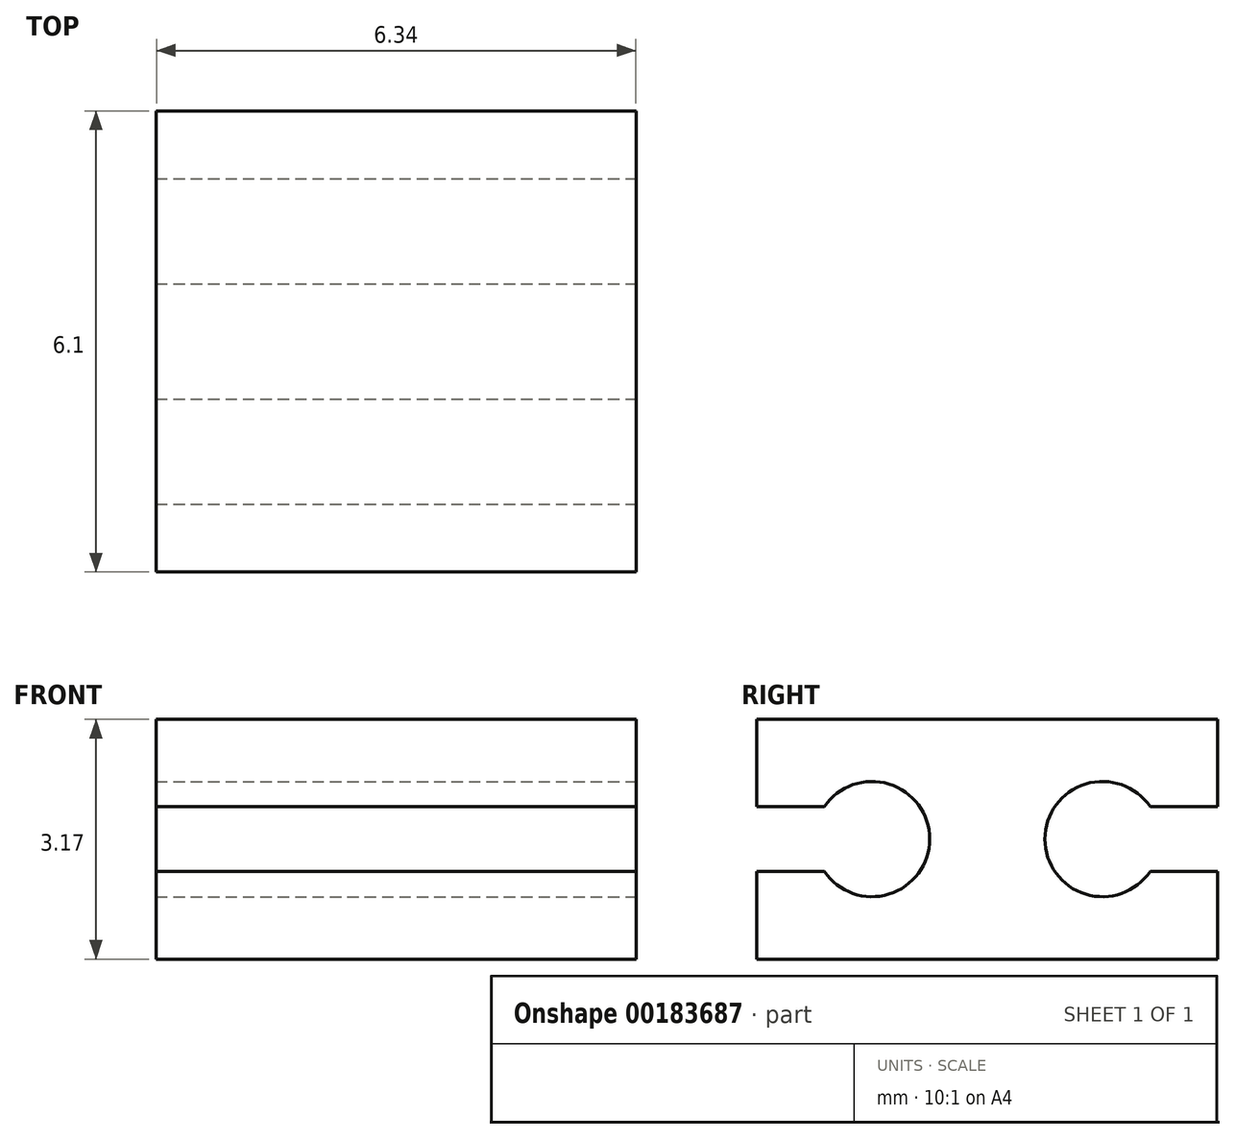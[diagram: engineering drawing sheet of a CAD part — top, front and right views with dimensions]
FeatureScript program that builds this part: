
annotation { "Feature Type Name" : "Feature", "Feature Type Description" : "" }
export const myFeature = defineFeature(function(context is Context, id is Id, definition is map)
    precondition{}
    {
        {
            var Q0;
            Q0=qCreatedBy(makeId("Top.planeOp"),FACE);
            var sketch = newSketch(context, id + "F0", { "sketchPlane" : qUnion([Q0])});
            skLineSegment(sketch, "E0.bottom", {"start": v(-3.17, 3.05) * mm, "end": v(3.18, 3.05) * mm});
            skLineSegment(sketch, "E0.top", {"start": v(-3.17, -3.05) * mm, "end": v(3.18, -3.05) * mm});
            skLineSegment(sketch, "E0.left", {"start": v(-3.17, 3.05) * mm, "end": v(-3.17, -3.05) * mm});
            skLineSegment(sketch, "E0.right", {"start": v(3.18, 3.05) * mm, "end": v(3.18, -3.05) * mm});
            skSolve(sketch);
        }
        {
            var Q0;
            Q0 = qSketchRegion(id + "F0", true);
            extrude(context, id + "F1", {"entities" : qUnion([Q0]), "depth" : 3.17 * mm});
        }
        {
            var Q0;
            Q0=makeQuery(id+"F1.opExtrude","SWEPT_FACE",FACE,{"disambiguationData":[OSD([sQuery(id+"F0.wireOp",EDGE,"E0.right")])]});
            var sketch = newSketch(context, id + "F2", { "sketchPlane" : qUnion([Q0])});
            skPoint(sketch, "E1", {"position": v(-1.52, 1.59) * mm});
            skPoint(sketch, "E2", {"position": v(1.52, 1.59) * mm});
            skArc(sketch, "E3", {"start": v(2.15, 2.01) * mm, "mid": v(0.76, 1.59) * mm, "end": v(2.15, 1.16) * mm});
            skArc(sketch, "E4", {"start": v(-2.15, 1.16) * mm, "mid": v(-0.76, 1.59) * mm, "end": v(-2.15, 2.01) * mm});
            skLineSegment(sketch, "E5", {"start": v(-2.15, 2.01) * mm, "end": v(-3.05, 2.01) * mm});
            skLineSegment(sketch, "E6", {"start": v(-2.15, 1.16) * mm, "end": v(-3.05, 1.16) * mm});
            skPoint(sketch, "E7.end.orphan", {"position": v(-3.05, 1.59) * mm});
            skPoint(sketch, "E8.end.orphan", {"position": v(0, 3.18) * mm});
            skPoint(sketch, "E8.start.orphan", {"position": v(0, 0) * mm});
            skLineSegment(sketch, "E9", {"start": v(2.15, 1.16) * mm, "end": v(3.05, 1.16) * mm});
            skLineSegment(sketch, "E10", {"start": v(2.15, 2.01) * mm, "end": v(3.05, 2.01) * mm});
            skPoint(sketch, "E11.start.orphan", {"position": v(3.05, 1.59) * mm});
            skSolve(sketch);
        }
        {
            var Q0;
            Q0=makeQuery(id+"F2.imprint","IMPRINT",FACE,{"disambiguationData":[TD([[makeQuery(id+"F2.imprint","IMPRINT",EDGE,{"derivedFrom":sQuery(id+"F2.wireOp",EDGE,"E3")}),1.0]])]});
            var Q1;
            Q1=makeQuery(id+"F2.imprint","IMPRINT",FACE,{"disambiguationData":[TD([[makeQuery(id+"F2.imprint","IMPRINT",EDGE,{"derivedFrom":sQuery(id+"F2.wireOp",EDGE,"E4")}),1.0]])]});
            extrude(context, id + "F3", {"entities" : qUnion([Q0, Q1]), "operationType" : NewBodyOperationType.REMOVE, "endBound" : BoundingType.THROUGH_ALL, "oppositeDirection" : true, "depth" : 6.35 * mm});
        }
    });
